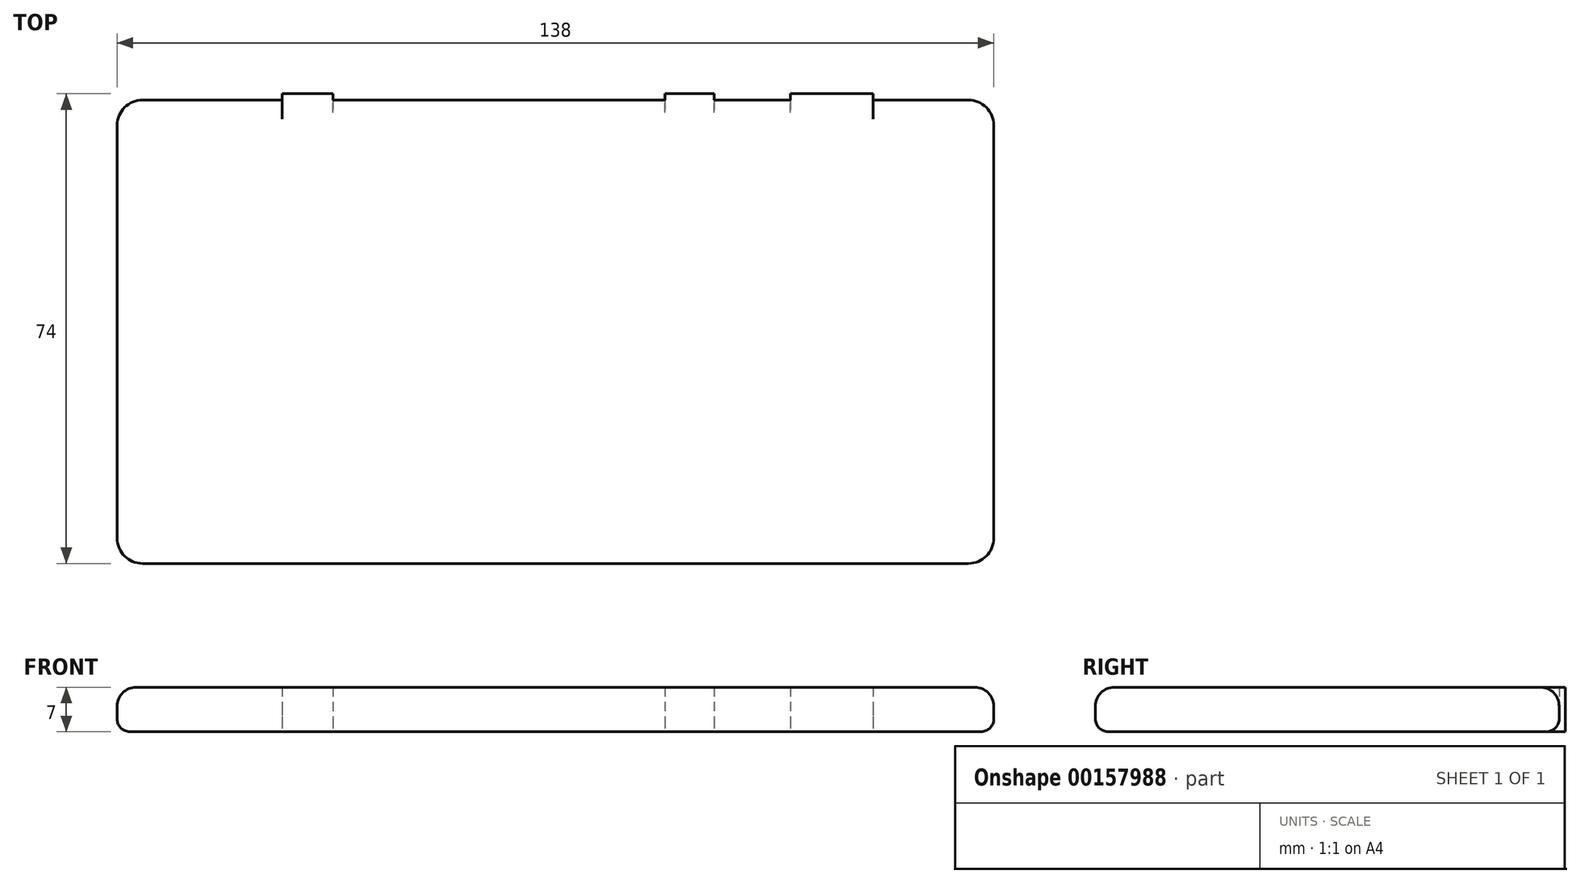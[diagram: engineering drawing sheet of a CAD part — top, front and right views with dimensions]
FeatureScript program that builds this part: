
annotation { "Feature Type Name" : "Feature", "Feature Type Description" : "" }
export const myFeature = defineFeature(function(context is Context, id is Id, definition is map)
    precondition{}
    {
        {
            var Q0;
            Q0=qCreatedBy(makeId("Top.planeOp"),FACE);
            var sketch = newSketch(context, id + "F0", { "sketchPlane" : qUnion([Q0])});
            skLineSegment(sketch, "E0.bottom", {"start": v(-62.87, 35.52) * mm, "end": v(67.13, 35.52) * mm});
            skLineSegment(sketch, "E0.top", {"start": v(-62.87, -37.48) * mm, "end": v(67.13, -37.48) * mm});
            skLineSegment(sketch, "E0.left", {"start": v(-66.87, 31.52) * mm, "end": v(-66.87, -33.48) * mm});
            skLineSegment(sketch, "E0.right", {"start": v(71.13, 31.52) * mm, "end": v(71.13, -33.48) * mm});
            skPoint(sketch, "E1.visualSharp", {"position": v(-66.87, 35.52) * mm});
            skArc(sketch, "E1.filletArc", {"start": v(-62.87, 35.52) * mm, "mid": v(-65.7, 34.35) * mm, "end": v(-66.87, 31.52) * mm});
            skPoint(sketch, "E2.visualSharp", {"position": v(71.13, 35.52) * mm});
            skArc(sketch, "E2.filletArc", {"start": v(71.13, 31.52) * mm, "mid": v(69.96, 34.35) * mm, "end": v(67.13, 35.52) * mm});
            skPoint(sketch, "E3.visualSharp", {"position": v(71.13, -37.48) * mm});
            skArc(sketch, "E3.filletArc", {"start": v(67.13, -37.48) * mm, "mid": v(69.96, -36.3) * mm, "end": v(71.13, -33.48) * mm});
            skPoint(sketch, "E4.visualSharp", {"position": v(-66.87, -37.48) * mm});
            skArc(sketch, "E4.filletArc", {"start": v(-66.87, -33.48) * mm, "mid": v(-65.7, -36.3) * mm, "end": v(-62.87, -37.48) * mm});
            skLineSegment(sketch, "E5.bottom", {"start": v(52.13, 35.52) * mm, "end": v(39.13, 35.52) * mm});
            skLineSegment(sketch, "E5.top", {"start": v(52.13, 36.52) * mm, "end": v(39.13, 36.52) * mm});
            skLineSegment(sketch, "E5.left", {"start": v(52.13, 35.52) * mm, "end": v(52.13, 36.52) * mm});
            skLineSegment(sketch, "E5.right", {"start": v(39.13, 35.52) * mm, "end": v(39.13, 36.52) * mm});
            skLineSegment(sketch, "E6.bottom", {"start": v(27.13, 35.52) * mm, "end": v(19.4, 35.52) * mm});
            skLineSegment(sketch, "E6.top", {"start": v(27.13, 36.52) * mm, "end": v(19.4, 36.52) * mm});
            skLineSegment(sketch, "E6.left", {"start": v(27.13, 35.52) * mm, "end": v(27.13, 36.52) * mm});
            skLineSegment(sketch, "E6.right", {"start": v(19.4, 35.52) * mm, "end": v(19.4, 36.52) * mm});
            skLineSegment(sketch, "E7.bottom", {"start": v(-40.87, 35.52) * mm, "end": v(-32.87, 35.52) * mm});
            skLineSegment(sketch, "E7.top", {"start": v(-40.87, 36.52) * mm, "end": v(-32.87, 36.52) * mm});
            skLineSegment(sketch, "E7.left", {"start": v(-40.87, 35.52) * mm, "end": v(-40.87, 36.52) * mm});
            skLineSegment(sketch, "E7.right", {"start": v(-32.87, 35.52) * mm, "end": v(-32.87, 36.52) * mm});
            skLineSegment(sketch, "E8.bottom", {"start": v(-66.87, 5.61) * mm, "end": v(-65.81, 5.61) * mm});
            skLineSegment(sketch, "E8.top", {"start": v(-66.87, -2.39) * mm, "end": v(-65.81, -2.39) * mm});
            skLineSegment(sketch, "E8.left", {"start": v(-66.87, 5.61) * mm, "end": v(-66.87, -2.39) * mm});
            skLineSegment(sketch, "E8.right", {"start": v(-65.47, 5.27) * mm, "end": v(-65.47, -2.04) * mm});
            skPoint(sketch, "E9.visualSharp", {"position": v(-65.47, 5.61) * mm});
            skArc(sketch, "E9.filletArc", {"start": v(-65.47, 5.27) * mm, "mid": v(-65.57, 5.51) * mm, "end": v(-65.81, 5.61) * mm});
            skPoint(sketch, "E10.visualSharp", {"position": v(-65.47, -2.39) * mm});
            skArc(sketch, "E10.filletArc", {"start": v(-65.81, -2.39) * mm, "mid": v(-65.57, -2.28) * mm, "end": v(-65.47, -2.04) * mm});
            skSolve(sketch);
        }
        {
            var Q0;
            Q0 = qSketchRegion(id + "F0", true);
            extrude(context, id + "F1", {"entities" : qUnion([Q0]), "depth" : 7 * mm});
        }
        {
            var Q0;
            Q0=makeQuery(id+"F1.opExtrude","CAP_EDGE",EDGE,{"disambiguationData":[OSD([sQuery(id+"F0.wireOp",EDGE,"E0.top")])],"isStart":false});
            fillet(context, id + "F2", {"entities" : qUnion([Q0]), "radius" : 3 * mm, "tangentPropagation" : true, "allowEdgeOverflow" : false});
        }
        {
            var Q0;
            Q0=makeQuery(id+"F1.opExtrude","CAP_EDGE",EDGE,{"disambiguationData":[OSD([sQuery(id+"F0.wireOp",EDGE,"E0.top")])],"isStart":true});
            var Q1;
            {var subQ0=sQuery(id+"F0.wireOp",EDGE,"E0.bottom");Q1=makeQuery(id+"F1.opExtrude","CAP_EDGE",EDGE,{"disambiguationData":[OSD([subQ0]),TDD([makeQuery(id+"F0.imprint","IMPRINT",EDGE,{"disambiguationData":[TD([[makeQuery(id+"F0.imprint","INTERSECT",VERTEX,{"derivedFrom":[subQ0,sQuery(id+"F0.wireOp",EDGE,"E6.bottom"),sQuery(id+"F0.wireOp",EDGE,"E6.right")]}),1.0]])],"derivedFrom":subQ0})])],"isStart":true});}
            var Q2;
            {var subQ0=sQuery(id+"F0.wireOp",EDGE,"E0.bottom");Q2=makeQuery(id+"F1.opExtrude","CAP_EDGE",EDGE,{"disambiguationData":[OSD([subQ0]),TDD([makeQuery(id+"F0.imprint","IMPRINT",EDGE,{"disambiguationData":[TD([[makeQuery(id+"F0.imprint","INTERSECT",VERTEX,{"derivedFrom":[subQ0,sQuery(id+"F0.wireOp",EDGE,"E5.bottom"),sQuery(id+"F0.wireOp",EDGE,"E5.right")]}),1.0]])],"derivedFrom":subQ0})])],"isStart":true});}
            fillet(context, id + "F3", {"entities" : qUnion([Q0, Q1, Q2]), "radius" : 2 * mm, "tangentPropagation" : true, "allowEdgeOverflow" : false});
        }
    });
